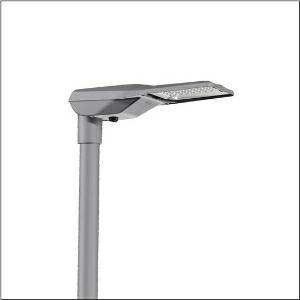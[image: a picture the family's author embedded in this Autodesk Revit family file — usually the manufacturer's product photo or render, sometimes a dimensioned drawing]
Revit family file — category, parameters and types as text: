
# Revit family: streetlight_sl_21_mini___st1_0ab_5xe2m33r08gb_46d4
name_source: partatom
category: Lighting Fixtures
units: mm (PartAtom-declared; Revit-internal decimal feet)

## family parameters
Cut with Voids When Loaded = No
Host = Face
Light Source = No
Part Type = Normal
Room Calculation Point = No
Round Connector Dimension = Use Diameter
Shared = No

## types (1)
- --- (1 x LED, 5230 lm, 40.4 W, 3000K)
    Apparent Load = 40 VA
    CIE Flux Codes = 38 73 97 100 100
    Color Rendering = 70
    Color Temperature = 3000K
    Default Elevation = 1800 mm
    Description = Streetlight SL 21 mini, mast luminaire, primary light control with lens, of PMMA, primary optical cover: cover, of toughened safety glass, transparent, light distribution: ST1.0aB, light emission: direct distribution, primary light characteristic: asymmetric, installation type: side-entry, post-top, LED, High Power LED, rated luminous flux: 5.230lm, luminous efficacy: 130lm/W, light colour: 730, colour temperature: 3000K, control gear: D4i, control: flexible luminous flux parameterisation, time-dependent luminous flux control, constant luminous flux control, overheat protection, pre-setting: logarithmic dimming characteristic, mains connection: 220..240V, AC, 50/60Hz, start of lifetime: 40W, end of service life: 41W, reduction: 19W, luminaire housing, of diecast aluminium, powder-coated, Siteco® metallic grey (DB 702S), corrosivity category C5 mid according to DIN EN ISO 12944, please order mast flange separately, inclination adjustable: 0°, 5°, 10°, 15°, sealing non-destructively replaceable, multi-level sealing system, length: 628mm, width: 235mm, height: 110mm, mast flange for spigot size: 42mm (side-entry): 5XC10008XM4, 60/48mm (side-entry/post-top): 5XC10108XM2, 76/60mm (side-entry/post-top): 5XC10108XM1, mounting height: 4..8m, Smart Interface below, protection rating (complete): IP66, insulation class (complete): insulation class II (safety insulation), certification: CE, ENEC, ENEC+, VDE, impact resistance: IK10, permissible operating ambient temperature for outdoor applications: -40..+50°C, standard-compliant lighting for roads and squares, packaging unit: 1 piece

Light Distribution: ST1.0aB
    Height = 110 mm
    Lamp = 1 x LED
    Lamp Light Flux = 5230 lm
    Lamp Power = 40.4 W
    Lamp count = 1
    Length = 625 mm
    Luminous efficacy = 129 lm/W
    Manufacturer = Siteco
    ModVariant = No
    Model = 5XE2M33R08GB
    Number of Poles = 1
    OnlyDefault = Yes
    Power Factor = 1
    Product Name = Streetlight SL 21 mini | ST1.0aB
    Product group = mast luminaire | pylon top
    ProductGroupID = 6100
    Protection Class = Protection class II
    Protection Degree = IP 66
    RLX_Detail_Level = 1
    RLX_Emergency_Light_Flux = 0 lm
    RLX_Emergency_Type = 0
    RLX_Emergency_Type_DB = No
    RlxData = <blob elided: 26281 chars, md5=f3f26a69>
    Socket = socket
    Standby Power = 0 W
    System Light Flux = 5230 lm
    System Power = 40 W
    Type Comments = factory setting: luminous flux: 100 % | dim-lin: 254 | 812 mA
    Type Image = l_1003516.jpg
    URL = http://relux.com
    VarID = @adj_203991
    Voltage = 0 V
    Weight = 0.00 kg
    Width = 234 mm

## geometry (parser evidence)
native form markers: Blend x4, Sweep x11
no freeform markers — native parametric forms only
